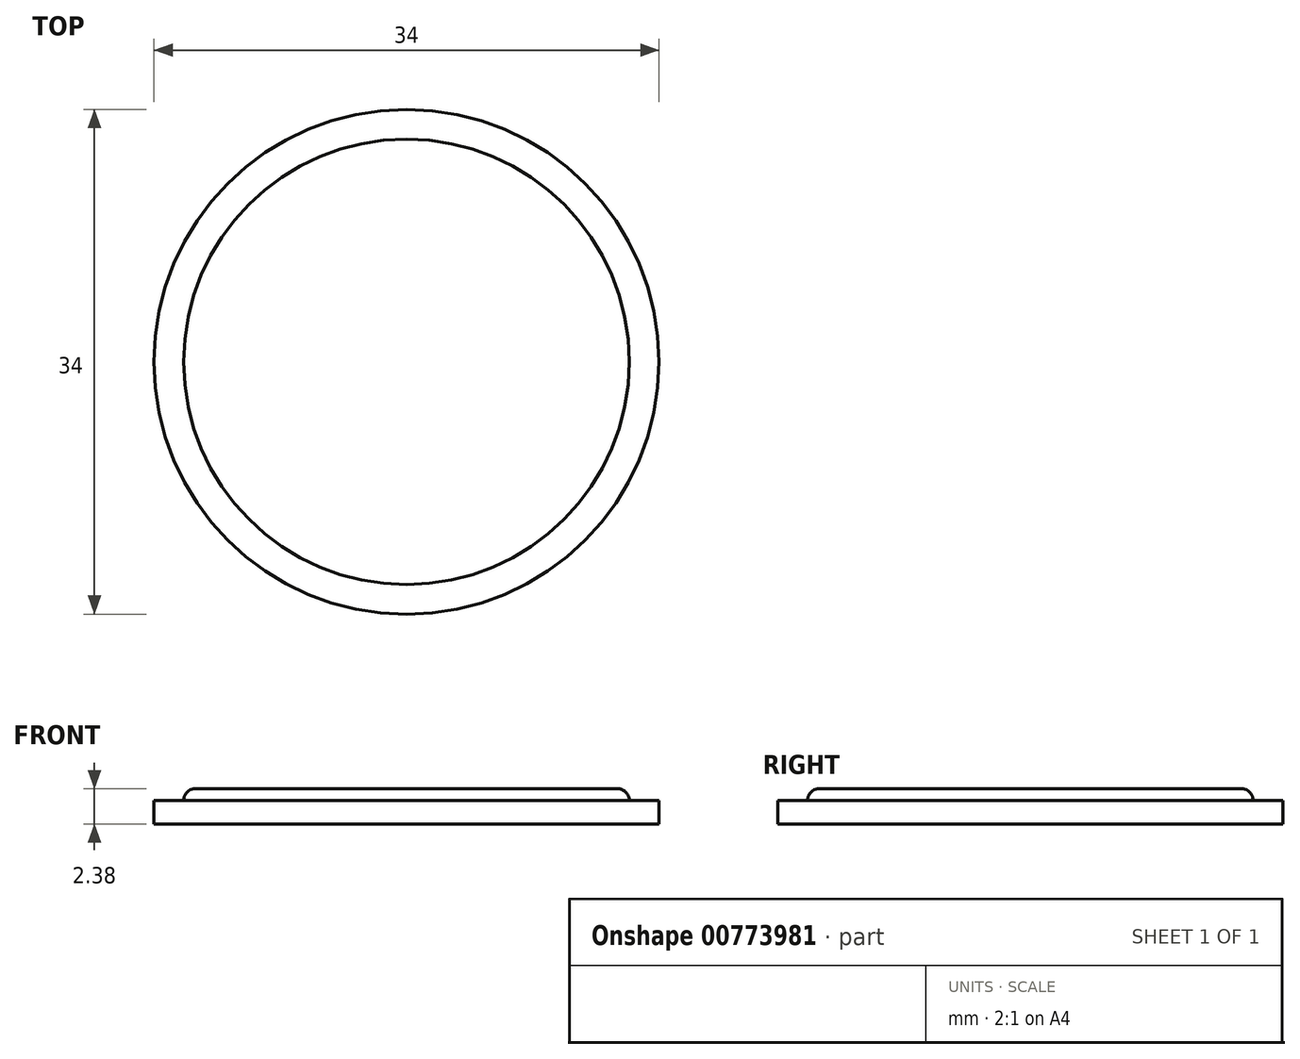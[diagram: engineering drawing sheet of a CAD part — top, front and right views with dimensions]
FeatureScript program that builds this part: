
annotation { "Feature Type Name" : "Feature", "Feature Type Description" : "" }
export const myFeature = defineFeature(function(context is Context, id is Id, definition is map)
    precondition{}
    {
        {
            assignVariable(context, id + "F0", {"name" : "InnerHeight", "anyValue" : 2.38 * mm});
        }
        {
            assignVariable(context, id + "F1", {"name" : "OutterHeight", "anyValue" : 1.59 * mm});
        }
        {
            var Q0;
            Q0=qCreatedBy(makeId("Top.planeOp"),FACE);
            var sketch = newSketch(context, id + "F2", { "sketchPlane" : qUnion([Q0])});
            skCircle(sketch, "E0", {"center": v(0, 0) * mm, "radius": 15 * mm});
            skCircle(sketch, "E1", {"center": v(0, 0) * mm, "radius": 17 * mm});
            skLineSegment(sketch, "E2", {"start": v(-17, 0) * mm, "end": v(17, 0) * mm});
            skSolve(sketch);
        }
        {
            var Q0;
            Q0=makeQuery(id+"F2.imprint","IMPRINT",FACE,{"disambiguationData":[TD([[makeQuery(id+"F2.imprint","IMPRINT",EDGE,{"derivedFrom":sQuery(id+"F2.wireOp",EDGE,"E0")}),1.0]])]});
            extrude(context, id + "F3", {"entities" : qUnion([Q0]), "depth" : getVariable(context, 'InnerHeight'), "offsetDistance" : 25.4 * mm});
        }
        {
            var Q0;
            Q0 = qSketchRegion(id + "F2", true);
            extrude(context, id + "F4", {"entities" : qUnion([Q0]), "operationType" : NewBodyOperationType.ADD, "depth" : getVariable(context, 'OutterHeight'), "offsetDistance" : 25.4 * mm});
        }
        {
            var Q0;
            Q0=makeQuery(id+"F3.opExtrude","CAP_EDGE",EDGE,{"disambiguationData":[OSD([sQuery(id+"F2.wireOp",EDGE,"E0")])],"isStart":false});
            fillet(context, id + "F5", {"entities" : qUnion([Q0]), "radius" : 0.8 * mm, "tangentPropagation" : true, "allowEdgeOverflow" : false});
        }
    });
